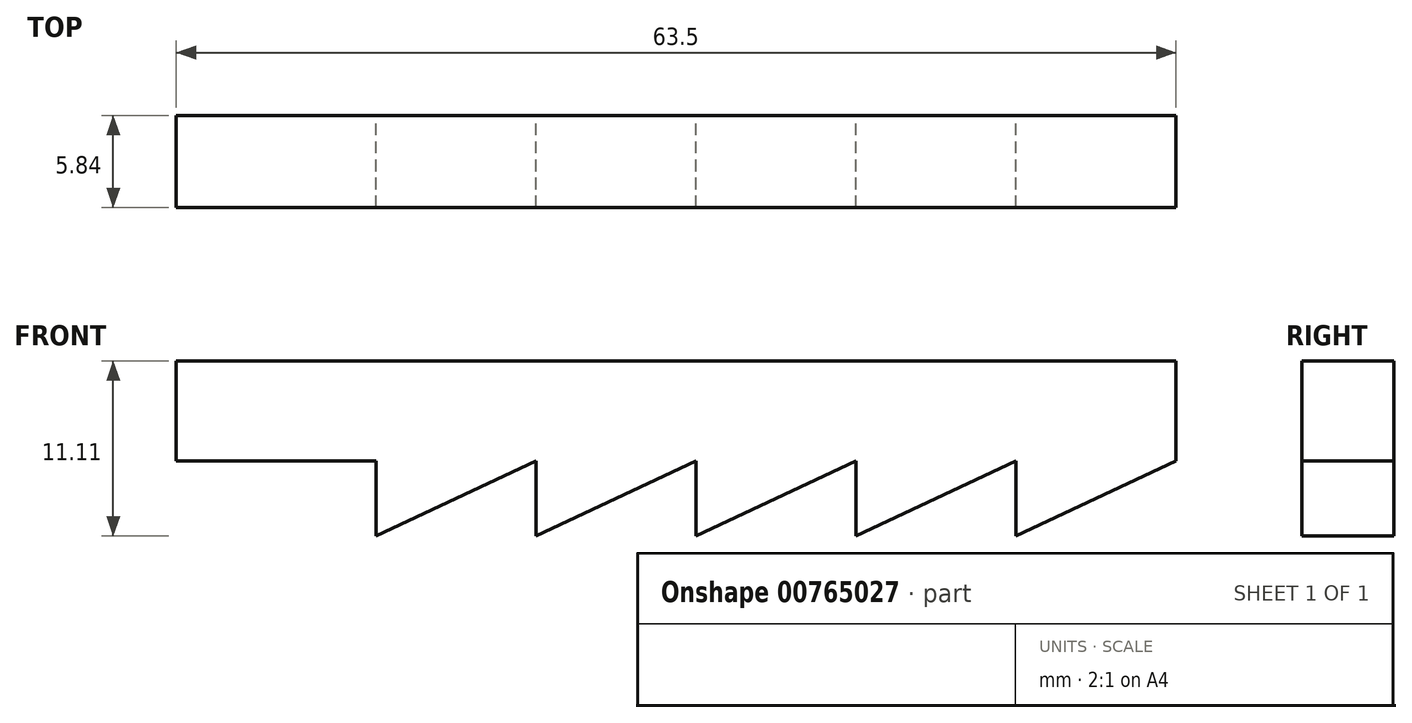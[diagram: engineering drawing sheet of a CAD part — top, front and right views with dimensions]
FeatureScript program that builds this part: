
annotation { "Feature Type Name" : "Feature", "Feature Type Description" : "" }
export const myFeature = defineFeature(function(context is Context, id is Id, definition is map)
    precondition{}
    {
        {
            var Q0;
            Q0=qCreatedBy(makeId("Front.planeOp"),FACE);
            var sketch = newSketch(context, id + "F0", { "sketchPlane" : qUnion([Q0])});
            skLineSegment(sketch, "E0.bottom", {"start": v(0, 0) * mm, "end": v(63.5, 0) * mm});
            skLineSegment(sketch, "E0.top", {"start": v(0, 6.35) * mm, "end": v(63.5, 6.35) * mm});
            skLineSegment(sketch, "E0.left", {"start": v(0, 0) * mm, "end": v(0, 6.35) * mm});
            skLineSegment(sketch, "E0.right", {"start": v(63.5, 0) * mm, "end": v(63.5, 6.35) * mm});
            skPoint(sketch, "E1.end.orphan", {"position": v(22.86, 0) * mm});
            skLineSegment(sketch, "E2", {"start": v(12.7, 0) * mm, "end": v(12.7, -4.76) * mm});
            skLineSegment(sketch, "E3", {"start": v(12.7, -4.76) * mm, "end": v(22.86, 0) * mm});
            skLineSegment(sketch, "E4.1.0.0", {"start": v(22.86, -4.76) * mm, "end": v(33.02, 0) * mm});
            skLineSegment(sketch, "E4.1.0.1", {"start": v(22.86, 0) * mm, "end": v(22.86, -4.76) * mm});
            skLineSegment(sketch, "E4.2.0.0", {"start": v(33.02, -4.76) * mm, "end": v(43.18, 0) * mm});
            skLineSegment(sketch, "E4.2.0.1", {"start": v(33.02, 0) * mm, "end": v(33.02, -4.76) * mm});
            skLineSegment(sketch, "E4.3.0.0", {"start": v(43.18, -4.76) * mm, "end": v(53.34, 0) * mm});
            skLineSegment(sketch, "E4.3.0.1", {"start": v(43.18, 0) * mm, "end": v(43.18, -4.76) * mm});
            skLineSegment(sketch, "E4.4.0.0", {"start": v(53.34, -4.76) * mm, "end": v(63.5, 0) * mm});
            skLineSegment(sketch, "E4.4.0.1", {"start": v(53.34, 0) * mm, "end": v(53.34, -4.76) * mm});
            skLineSegment(sketch, "E4.direction1", {"start": v(12.7, -4.76) * mm, "end": v(22.86, -4.76) * mm, "construction": true});
            skSolve(sketch);
        }
        {
            var Q0;
            Q0 = qSketchRegion(id + "F0", true);
            extrude(context, id + "F1", {"entities" : qUnion([Q0]), "depth" : 5.84 * mm, "offsetDistance" : 25.4 * mm});
        }
    });
